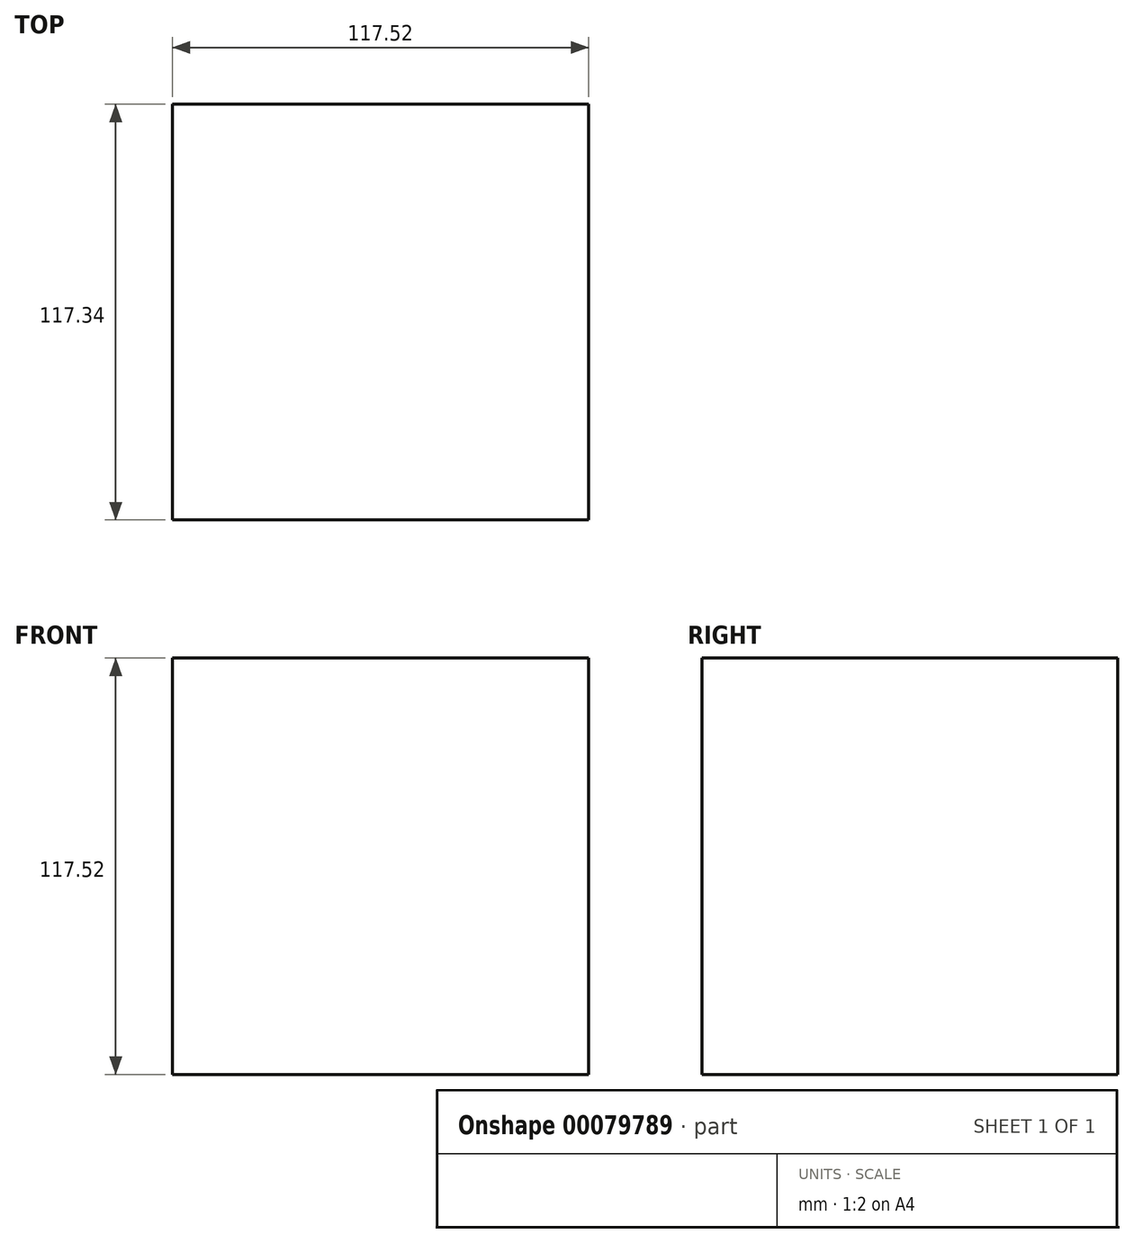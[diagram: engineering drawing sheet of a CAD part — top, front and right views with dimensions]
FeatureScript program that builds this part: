
annotation { "Feature Type Name" : "Feature", "Feature Type Description" : "" }
export const myFeature = defineFeature(function(context is Context, id is Id, definition is map)
    precondition{}
    {
        {
            var Q0;
            Q0=qCreatedBy(makeId("Front.planeOp"),FACE);
            var sketch = newSketch(context, id + "F0", { "sketchPlane" : qUnion([Q0])});
            skArc(sketch, "E0", {"start": v(0, -58.76) * mm, "mid": v(58.76, 0) * mm, "end": v(0, 58.76) * mm});
            skLineSegment(sketch, "E1", {"start": v(0, 0) * mm, "end": v(0, 12.98) * mm});
            skLineSegment(sketch, "E2.bottom", {"start": v(58.76, 58.76) * mm, "end": v(-58.76, 58.76) * mm});
            skLineSegment(sketch, "E2.top", {"start": v(58.76, -58.76) * mm, "end": v(-58.76, -58.76) * mm});
            skLineSegment(sketch, "E2.left", {"start": v(58.76, 58.76) * mm, "end": v(58.76, -58.76) * mm});
            skLineSegment(sketch, "E2.right", {"start": v(-58.76, 58.76) * mm, "end": v(-58.76, -58.76) * mm});
            skSolve(sketch);
        }
        {
            var Q0;
            Q0=sQuery(id+"F0.wireOp",EDGE,"E0");
            var Q1;
            Q1=sQuery(id+"F0.wireOp",EDGE,"E1");
            revolve(context, id + "F1", {"bodyType" : ToolBodyType.SURFACE, "surfaceEntities" : qUnion([Q0]), "axis" : qUnion([Q1]), "revolveType" : RevolveType.FULL});
        }
        {
            var Q0;
            {var subQ3=sQuery(id+"F0.wireOp",EDGE,"E2.right");Q0=makeQuery(id+"F0.imprint","IMPRINT",FACE,{"disambiguationData":[TD([[makeQuery(id+"F0.imprint","IMPRINT",EDGE,{"derivedFrom":subQ3}),1.0]])]});}
            var Q1;
            {var subQ0=sQuery(id+"F0.wireOp",EDGE,"E2.bottom");var subQ1=sQuery(id+"F0.wireOp",EDGE,"E0");var subQ2=makeQuery(id+"F0.imprint","INTERSECT",VERTEX,{"derivedFrom":[subQ1,subQ0]});Q1=makeQuery(id+"F0.imprint","IMPRINT",FACE,{"disambiguationData":[TD([[makeQuery(id+"F0.imprint","IMPRINT",EDGE,{"disambiguationData":[TD([[subQ2,1.0]])],"derivedFrom":subQ1}),-1.0]])]});}
            var Q2;
            {var subQ0=sQuery(id+"F0.wireOp",EDGE,"E2.top");var subQ1=sQuery(id+"F0.wireOp",EDGE,"E0");var subQ2=makeQuery(id+"F0.imprint","INTERSECT",VERTEX,{"derivedFrom":[subQ1,subQ0]});Q2=makeQuery(id+"F0.imprint","IMPRINT",FACE,{"disambiguationData":[TD([[makeQuery(id+"F0.imprint","IMPRINT",EDGE,{"disambiguationData":[TD([[subQ2,-1.0]])],"derivedFrom":subQ1}),-1.0]])]});}
            extrude(context, id + "F2", {"entities" : qUnion([Q0, Q1, Q2]), "endBound" : BoundingType.SYMMETRIC, "depth" : 117.35 * mm});
        }
    });
